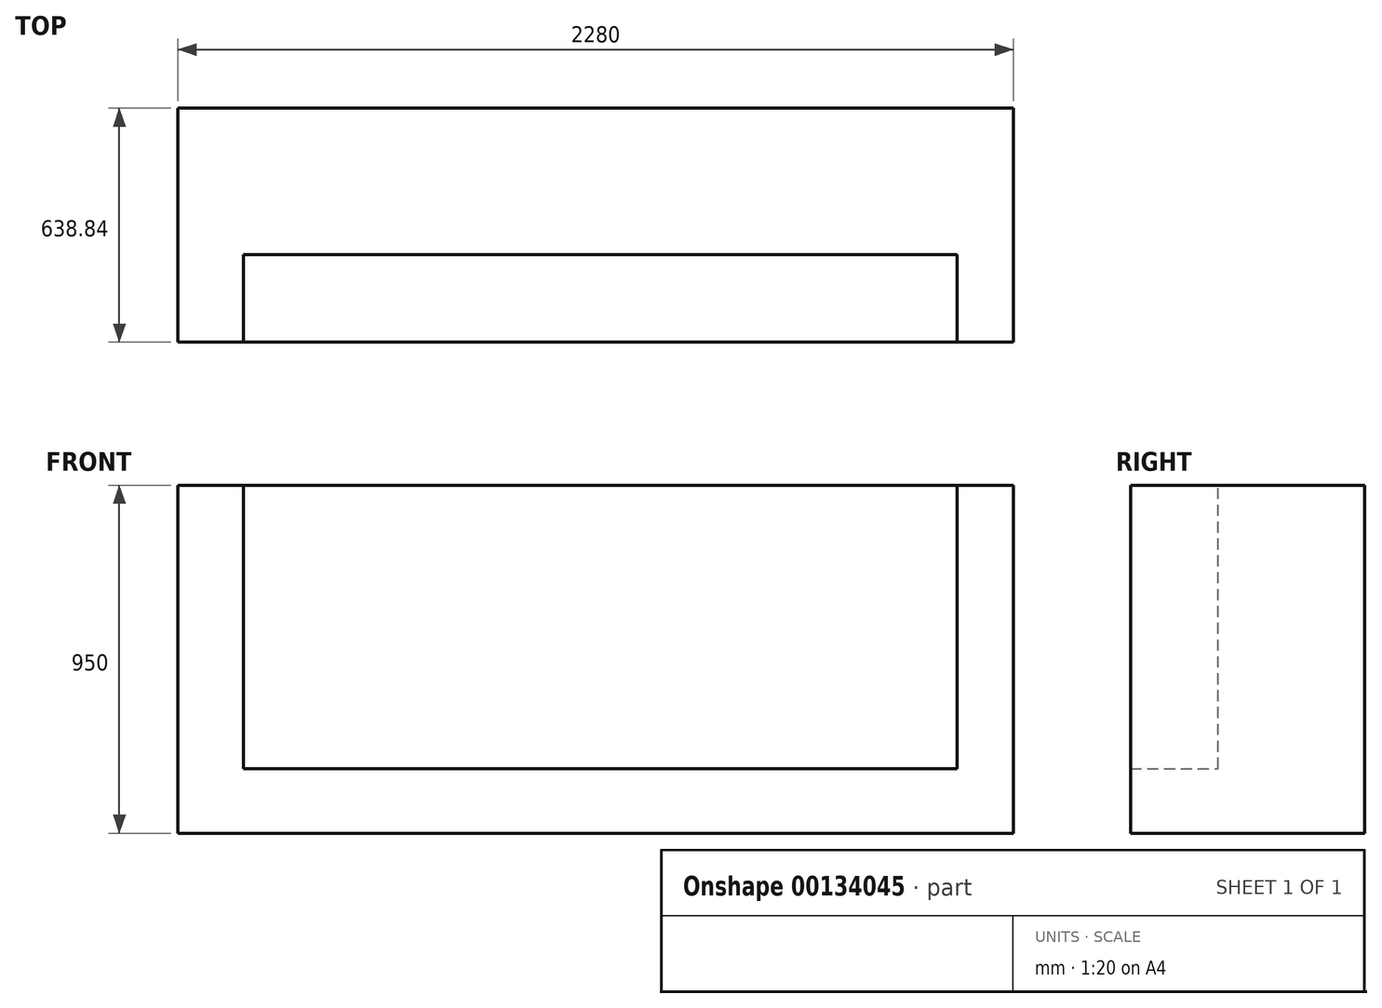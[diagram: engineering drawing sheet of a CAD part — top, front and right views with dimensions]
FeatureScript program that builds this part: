
annotation { "Feature Type Name" : "Feature", "Feature Type Description" : "" }
export const myFeature = defineFeature(function(context is Context, id is Id, definition is map)
    precondition{}
    {
        {
            var Q0;
            Q0=qCreatedBy(makeId("Front.planeOp"),FACE);
            var sketch = newSketch(context, id + "F0", { "sketchPlane" : qUnion([Q0])});
            skLineSegment(sketch, "E0.bottom", {"start": v(0, 0) * mm, "end": v(2280, 0) * mm});
            skLineSegment(sketch, "E0.top", {"start": v(0, 950) * mm, "end": v(2280, 950) * mm});
            skLineSegment(sketch, "E0.left", {"start": v(0, 0) * mm, "end": v(0, 950) * mm});
            skLineSegment(sketch, "E0.right", {"start": v(2280, 0) * mm, "end": v(2280, 950) * mm});
            skSolve(sketch);
        }
        {
            var Q0;
            Q0=makeQuery(id+"F0.imprint","IMPRINT",FACE,{"disambiguationData":[TD([[makeQuery(id+"F0.imprint","IMPRINT",EDGE,{"derivedFrom":sQuery(id+"F0.wireOp",EDGE,"E0.bottom")}),1.0]])]});
            extrude(context, id + "F1", {"entities" : qUnion([Q0]), "depth" : 400 * mm});
        }
        {
            var Q0;
            Q0=makeQuery(id+"F1.opExtrude","CAP_FACE",FACE,{"disambiguationData":[OSD([sQuery(id+"F0.wireOp",EDGE,"E0.bottom"),sQuery(id+"F0.wireOp",EDGE,"E0.top"),sQuery(id+"F0.wireOp",EDGE,"E0.left"),sQuery(id+"F0.wireOp",EDGE,"E0.right")])],"isStart":false});
            var sketch = newSketch(context, id + "F2", { "sketchPlane" : qUnion([Q0])});
            skLineSegment(sketch, "E1.bottom", {"start": v(0, 0) * mm, "end": v(2280, 0) * mm});
            skLineSegment(sketch, "E1.top", {"start": v(0, 176.37) * mm, "end": v(2280, 176.37) * mm});
            skLineSegment(sketch, "E1.left", {"start": v(0, 0) * mm, "end": v(0, 176.37) * mm});
            skLineSegment(sketch, "E1.right", {"start": v(2280, 0) * mm, "end": v(2280, 176.37) * mm});
            skLineSegment(sketch, "E2.bottom", {"start": v(0, 0) * mm, "end": v(179.1, 0) * mm});
            skLineSegment(sketch, "E2.top", {"start": v(0, 950) * mm, "end": v(179.1, 950) * mm});
            skLineSegment(sketch, "E2.left", {"start": v(0, 0) * mm, "end": v(0, 950) * mm});
            skLineSegment(sketch, "E2.right", {"start": v(179.1, 0) * mm, "end": v(179.1, 950) * mm});
            skLineSegment(sketch, "E3.bottom", {"start": v(2280, 0) * mm, "end": v(2127.01, 0) * mm});
            skLineSegment(sketch, "E3.top", {"start": v(2280, 950) * mm, "end": v(2127.01, 950) * mm});
            skLineSegment(sketch, "E3.left", {"start": v(2280, 0) * mm, "end": v(2280, 950) * mm});
            skLineSegment(sketch, "E3.right", {"start": v(2127.01, 0) * mm, "end": v(2127.01, 950) * mm});
            skSolve(sketch);
        }
        {
            var Q0;
            {var subQ5=sQuery(id+"F2.wireOp",EDGE,"E2.top");Q0=makeQuery(id+"F2.imprint","IMPRINT",FACE,{"disambiguationData":[TD([[makeQuery(id+"F2.imprint","IMPRINT",EDGE,{"derivedFrom":subQ5}),-1.0]])]});}
            var Q1;
            {var subQ5=sQuery(id+"F2.wireOp",EDGE,"E2.bottom");Q1=makeQuery(id+"F2.imprint","IMPRINT",FACE,{"disambiguationData":[TD([[makeQuery(id+"F2.imprint","IMPRINT",EDGE,{"derivedFrom":subQ5}),1.0]])]});}
            var Q2;
            {var subQ0=sQuery(id+"F2.wireOp",EDGE,"E1.bottom");Q2=makeQuery(id+"F2.imprint","IMPRINT",FACE,{"disambiguationData":[TD([[makeQuery(id+"F2.imprint","IMPRINT",EDGE,{"derivedFrom":subQ0}),1.0]])]});}
            var Q3;
            {var subQ5=sQuery(id+"F2.wireOp",EDGE,"E3.bottom");Q3=makeQuery(id+"F2.imprint","IMPRINT",FACE,{"disambiguationData":[TD([[makeQuery(id+"F2.imprint","IMPRINT",EDGE,{"derivedFrom":subQ5}),1.0]])]});}
            var Q4;
            {var subQ5=sQuery(id+"F2.wireOp",EDGE,"E3.top");Q4=makeQuery(id+"F2.imprint","IMPRINT",FACE,{"disambiguationData":[TD([[makeQuery(id+"F2.imprint","IMPRINT",EDGE,{"derivedFrom":subQ5}),-1.0]])]});}
            extrude(context, id + "F3", {"entities" : qUnion([Q0, Q1, Q2, Q3, Q4]), "operationType" : NewBodyOperationType.ADD, "depth" : 238.84 * mm});
        }
    });
